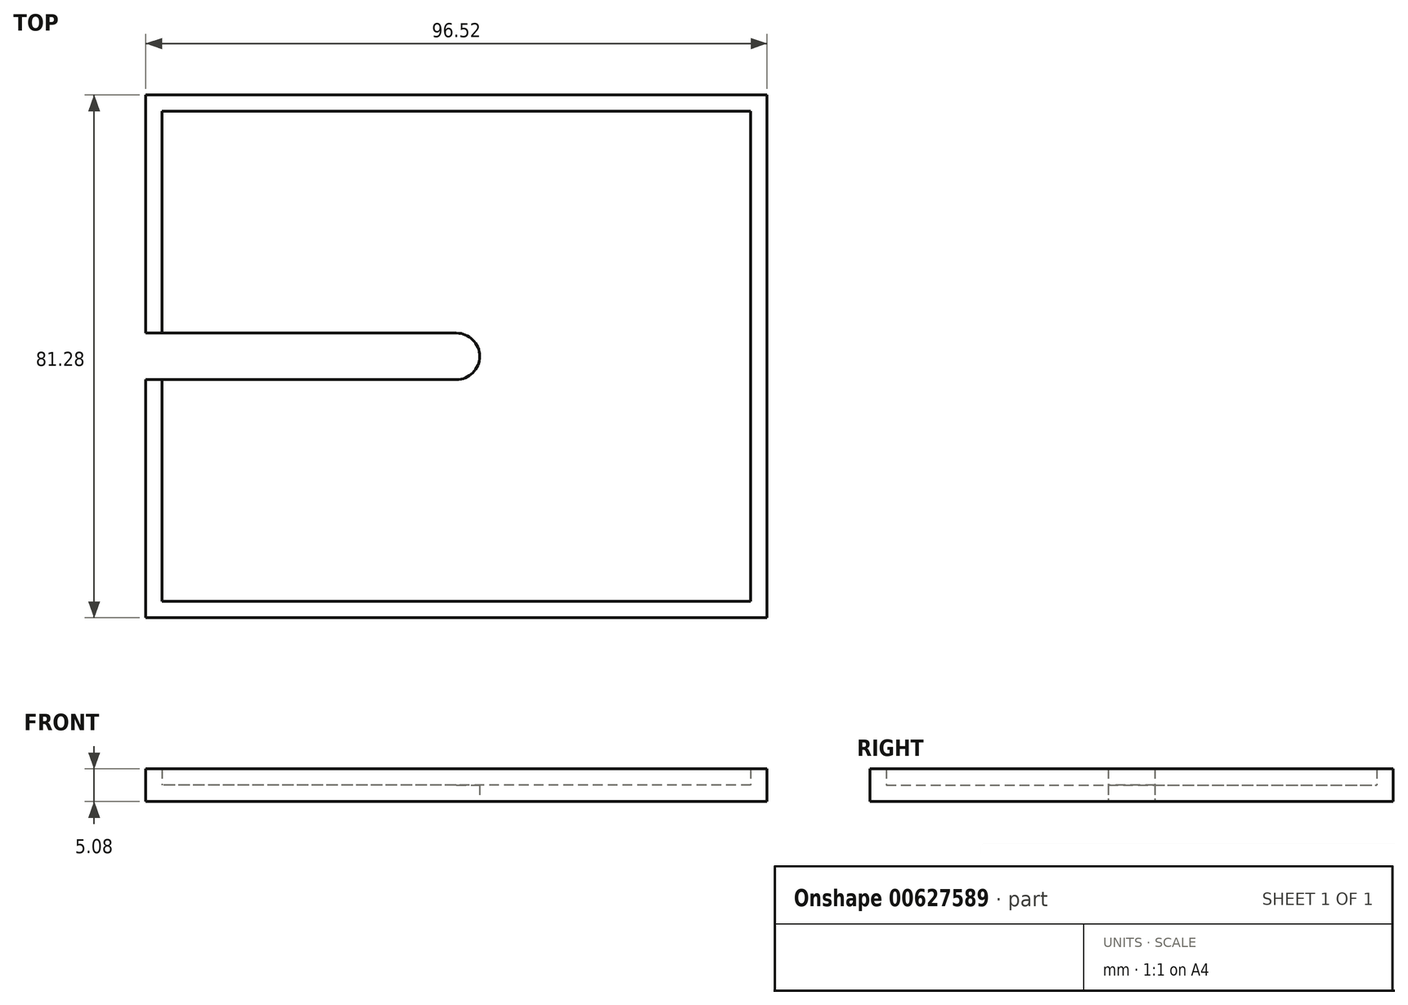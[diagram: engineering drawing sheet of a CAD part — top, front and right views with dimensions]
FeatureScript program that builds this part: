
annotation { "Feature Type Name" : "Feature", "Feature Type Description" : "" }
export const myFeature = defineFeature(function(context is Context, id is Id, definition is map)
    precondition{}
    {
        {
            var Q0;
            Q0=qCreatedBy(makeId("Front.planeOp"),FACE);
            var sketch = newSketch(context, id + "F0", { "sketchPlane" : qUnion([Q0])});
            skLineSegment(sketch, "E0.bottom", {"start": v(48.26, 2.54) * mm, "end": v(-48.26, 2.54) * mm});
            skLineSegment(sketch, "E0.top", {"start": v(48.26, -2.54) * mm, "end": v(-48.26, -2.54) * mm});
            skLineSegment(sketch, "E0.left", {"start": v(48.26, 2.54) * mm, "end": v(48.26, -2.54) * mm});
            skLineSegment(sketch, "E0.right", {"start": v(-48.26, 2.54) * mm, "end": v(-48.26, -2.54) * mm});
            skPoint(sketch, "E0.middle", {"position": v(0, 0) * mm});
            skSolve(sketch);
        }
        {
            var Q0;
            Q0 = qSketchRegion(id + "F0", true);
            extrude(context, id + "F1", {"entities" : qUnion([Q0]), "endBound" : BoundingType.SYMMETRIC, "depth" : 81.28 * mm, "offsetDistance" : 25.4 * mm});
        }
        {
            var Q0;
            Q0=makeQuery(id+"F1.opExtrude","SWEPT_FACE",FACE,{"disambiguationData":[OSD([sQuery(id+"F0.wireOp",EDGE,"E0.bottom")])]});
            shell(context, id + "F2", {"entities" : qUnion([Q0]), "thickness" : 2.54 * mm});
        }
        {
            var Q0;
            Q0=makeQuery(id+"F1.opExtrude","SWEPT_FACE",FACE,{"disambiguationData":[OSD([sQuery(id+"F0.wireOp",EDGE,"E0.top")])]});
            var sketch = newSketch(context, id + "F3", { "sketchPlane" : qUnion([Q0])});
            skLineSegment(sketch, "E1.left", {"start": v(0, 3.61) * mm, "end": v(0, -3.61) * mm});
            skPoint(sketch, "E1.middle", {"position": v(-48.26, 0) * mm});
            skLineSegment(sketch, "E2", {"start": v(-48.26, 3.61) * mm, "end": v(-48.26, -3.61) * mm});
            skLineSegment(sketch, "E3.bottom", {"start": v(-48.26, -3.61) * mm, "end": v(0, -3.61) * mm});
            skLineSegment(sketch, "E3.top", {"start": v(-48.26, 3.61) * mm, "end": v(0, 3.61) * mm});
            skLineSegment(sketch, "E3.left", {"start": v(-48.26, -3.61) * mm, "end": v(-48.26, 3.61) * mm});
            skLineSegment(sketch, "E3.right", {"start": v(0, -3.61) * mm, "end": v(0, 3.61) * mm});
            skArc(sketch, "E4", {"start": v(0, -3.61) * mm, "mid": v(3.61, 0) * mm, "end": v(0, 3.61) * mm});
            skSolve(sketch);
        }
        {
            var Q0;
            Q0 = qSketchRegion(id + "F3", true);
            extrude(context, id + "F4", {"entities" : qUnion([Q0]), "operationType" : NewBodyOperationType.REMOVE, "endBound" : BoundingType.UP_TO_NEXT, "oppositeDirection" : true, "depth" : 25.4 * mm, "offsetDistance" : 25.4 * mm});
        }
    });
